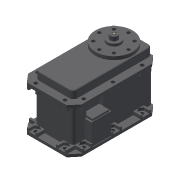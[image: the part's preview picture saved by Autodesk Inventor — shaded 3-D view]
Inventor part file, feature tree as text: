
AUTODESK INVENTOR PART (.ipt)
format: ipt  version: 2020 (Build 240168000, 168)  size: 675,328 bytes
history: native  units: mm (DEFAULTED — no unit token found)
features: other x5, sketch x2, extrude x1
ambient origin geometry x8: Origin, YZ Plane, XZ Plane, XY Plane, X Axis, Y Axis, Z Axis, Center Point
bodies: Body1 (feature_tree)
feature tree (8):
  other  "솔리드1"
  other  "기준1"
  other  "작업 평면1"
  other  "작업 평면2"
  sketch  "스케치1"
  other  "작업 평면3"
  extrude  "돌출1"  [1 undecoded]
  sketch  "스케치2"
note: 1 required parameter value undecoded (feature->parameter linkage not recoverable at this tier; creation-order binding heuristic only, values carry confidence <= 0.55)
